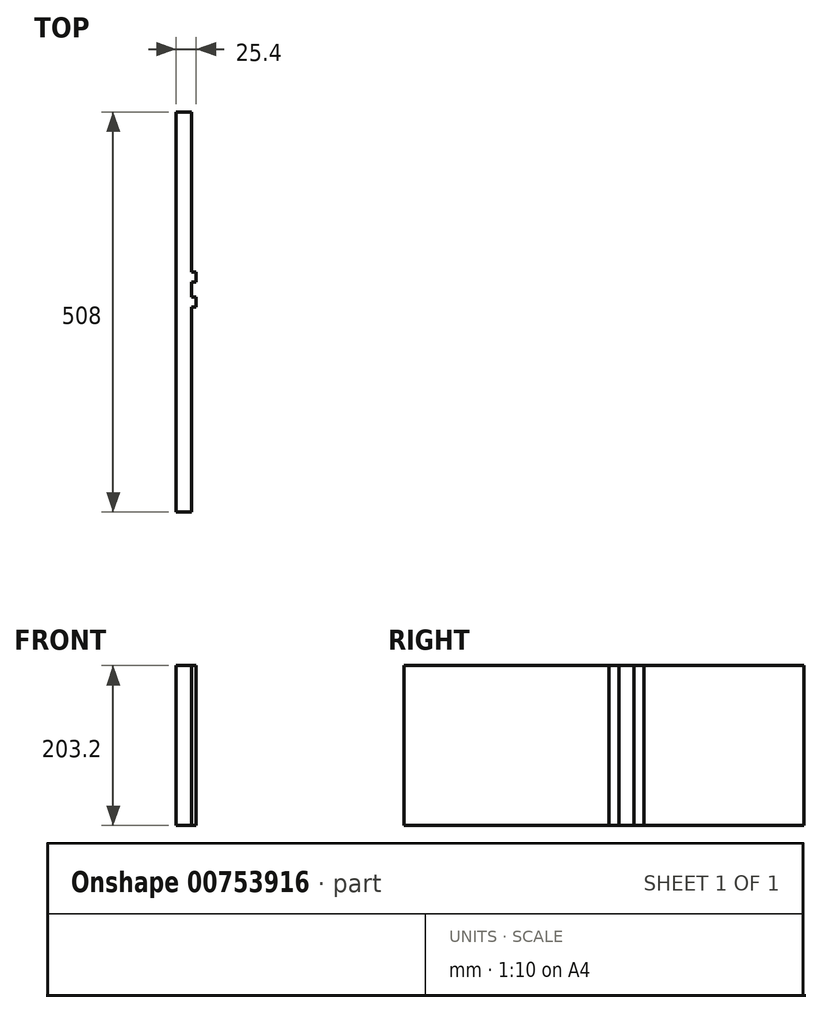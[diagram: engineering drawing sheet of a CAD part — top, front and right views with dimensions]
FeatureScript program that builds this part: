
annotation { "Feature Type Name" : "Feature", "Feature Type Description" : "" }
export const myFeature = defineFeature(function(context is Context, id is Id, definition is map)
    precondition{}
    {
        {
            var Q0;
            Q0=qCreatedBy(makeId("Right.planeOp"),FACE);
            var sketch = newSketch(context, id + "F0", { "sketchPlane" : qUnion([Q0])});
            skLineSegment(sketch, "E0.bottom", {"start": v(254, -101.6) * mm, "end": v(-254, -101.6) * mm});
            skLineSegment(sketch, "E0.top", {"start": v(254, 101.6) * mm, "end": v(-254, 101.6) * mm});
            skLineSegment(sketch, "E0.left", {"start": v(254, -101.6) * mm, "end": v(254, 101.6) * mm});
            skLineSegment(sketch, "E0.right", {"start": v(-254, -101.6) * mm, "end": v(-254, 101.6) * mm});
            skPoint(sketch, "E0.middle", {"position": v(0, 0) * mm});
            skLineSegment(sketch, "E1", {"start": v(254, 101.6) * mm, "end": v(50.8, 101.6) * mm});
            skLineSegment(sketch, "E2", {"start": v(50.8, 101.6) * mm, "end": v(38.1, 101.6) * mm});
            skLineSegment(sketch, "E3", {"start": v(38.1, 101.6) * mm, "end": v(19.05, 101.6) * mm});
            skLineSegment(sketch, "E4", {"start": v(19.05, 101.6) * mm, "end": v(6.35, 101.6) * mm});
            skLineSegment(sketch, "E5.bottom", {"start": v(6.35, 101.6) * mm, "end": v(19.05, 101.6) * mm});
            skLineSegment(sketch, "E5.top", {"start": v(6.35, -101.6) * mm, "end": v(19.05, -101.6) * mm});
            skLineSegment(sketch, "E5.left", {"start": v(6.35, 101.6) * mm, "end": v(6.35, -101.6) * mm});
            skLineSegment(sketch, "E5.right", {"start": v(19.05, 101.6) * mm, "end": v(19.05, -101.6) * mm});
            skLineSegment(sketch, "E6.bottom", {"start": v(38.1, 101.6) * mm, "end": v(50.8, 101.6) * mm});
            skLineSegment(sketch, "E6.top", {"start": v(38.1, -101.6) * mm, "end": v(50.8, -101.6) * mm});
            skLineSegment(sketch, "E6.left", {"start": v(38.1, 101.6) * mm, "end": v(38.1, -101.6) * mm});
            skLineSegment(sketch, "E6.right", {"start": v(50.8, 101.6) * mm, "end": v(50.8, -101.6) * mm});
            skSolve(sketch);
        }
        {
            var Q0;
            {var subQ0=sQuery(id+"F0.wireOp",EDGE,"E0.left");Q0=makeQuery(id+"F0.imprint","IMPRINT",FACE,{"disambiguationData":[TD([[makeQuery(id+"F0.imprint","IMPRINT",EDGE,{"derivedFrom":subQ0}),1.0]])]});}
            var Q1;
            {var subQ2=sQuery(id+"F0.wireOp",EDGE,"E5.right");Q1=makeQuery(id+"F0.imprint","IMPRINT",FACE,{"disambiguationData":[TD([[makeQuery(id+"F0.imprint","IMPRINT",EDGE,{"derivedFrom":subQ2}),1.0]])]});}
            var Q2;
            {var subQ0=sQuery(id+"F0.wireOp",EDGE,"E5.left");Q2=makeQuery(id+"F0.imprint","IMPRINT",FACE,{"disambiguationData":[TD([[makeQuery(id+"F0.imprint","IMPRINT",EDGE,{"derivedFrom":subQ0}),1.0]])]});}
            var Q3;
            {var subQ2=sQuery(id+"F0.wireOp",EDGE,"E0.right");Q3=makeQuery(id+"F0.imprint","IMPRINT",FACE,{"disambiguationData":[TD([[makeQuery(id+"F0.imprint","IMPRINT",EDGE,{"derivedFrom":subQ2}),-1.0]])]});}
            var Q4;
            {var subQ0=sQuery(id+"F0.wireOp",EDGE,"E6.left");Q4=makeQuery(id+"F0.imprint","IMPRINT",FACE,{"disambiguationData":[TD([[makeQuery(id+"F0.imprint","IMPRINT",EDGE,{"derivedFrom":subQ0}),1.0]])]});}
            extrude(context, id + "F1", {"entities" : qUnion([Q0, Q1, Q2, Q3, Q4]), "oppositeDirection" : true, "depth" : 19.05 * mm, "offsetDistance" : 25.4 * mm});
        }
        {
            var Q0;
            {var subQ0=sQuery(id+"F0.wireOp",EDGE,"E6.left");Q0=makeQuery(id+"F0.imprint","IMPRINT",FACE,{"disambiguationData":[TD([[makeQuery(id+"F0.imprint","IMPRINT",EDGE,{"derivedFrom":subQ0}),1.0]])]});}
            var Q1;
            {var subQ0=sQuery(id+"F0.wireOp",EDGE,"E5.left");Q1=makeQuery(id+"F0.imprint","IMPRINT",FACE,{"disambiguationData":[TD([[makeQuery(id+"F0.imprint","IMPRINT",EDGE,{"derivedFrom":subQ0}),1.0]])]});}
            extrude(context, id + "F2", {"entities" : qUnion([Q0, Q1]), "operationType" : NewBodyOperationType.ADD, "depth" : 6.35 * mm, "offsetDistance" : 25.4 * mm});
        }
    });
